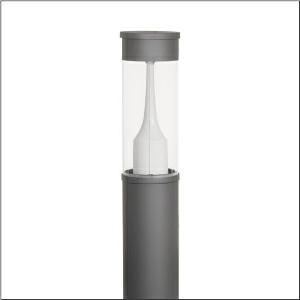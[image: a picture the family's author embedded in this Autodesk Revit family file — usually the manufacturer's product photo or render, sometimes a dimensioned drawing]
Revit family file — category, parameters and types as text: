
# Revit family: city-light_400_iq___st1_2a_5xa5305kf14h_7e7c
name_source: partatom
category: Lighting Fixtures
units: mm (PartAtom-declared; Revit-internal decimal feet)

## family parameters
Cut with Voids When Loaded = No
Host = Face
Light Source = No
Part Type = Normal
Room Calculation Point = No
Round Connector Dimension = Use Diameter
Shared = No

## types (1)
- --- (1 x LED, 1540 lm, 10 W, 4000K)
    Apparent Load = 10 VA
    CIE Flux Codes = 22 61 93 96 100
    Color Rendering = 70
    Color Temperature = 4000K
    Default Elevation = 1800 mm
    Description = City-Light 400 iQ, light pillar, Module 540 iQ-SR, primary light control with 3 zone facetted reflector, of plastic, silver coated, highly specular, structured, primary optical cover: cover, of PMMA, transparent, partly coated, light distribution: ST1.2a, primary light characteristic: asymmetric, LED, High Power LED, rated luminous flux: 1.540lm, luminous efficacy: 154lm/W, light colour: 740, colour temperature: 4000K, control gear: iQ Street-Remote, control: pre-setting: logarithmic dimming characteristic, Street-Remote, Auto-Match, Temp-Guard, Lumen-Switch, Night-Set, Smart-Wire, Light-Fading, Desk-Remote (wireless, voltage-free reading and setting of iQ features in the workshop via application-optimized NFC function/RFID function), optimised constant luminous flux control (CLO 2.0), with terminal, 6-pole, max. 2.5mm², mains connection: 230..240V, AC, 50/60Hz, start of lifetime: 10W, end of service life: 10W, reduction: 5W, luminaire housing, cylindrical, of extruded aluminium section, coated, Siteco® metallic grey (DB 702S), length: 4.694mm, diameter: 200mm, Module 540 iQ-SR, traffic white (RAL 9016), equipment: standard, protection rating (complete): IP65, insulation class (complete): insulation class II (safety insulation), certification: CE, ENEC, VDE, packaging unit: 1 piece

Light Distribution: ST1.2a
    Height = 500 mm
    Lamp = 1 x LED
    Lamp Light Flux = 1540 lm
    Lamp Power = 10 W
    Lamp count = 1
    Length = 200 mm  [stored 0.656168 ft]
    Luminous efficacy = 154 lm/W
    Manufacturer = Siteco
    ModVariant = No
    Model = 5XA5305KF14H
    Mounting Place = Floor
    Mounting Type = Freestanding
    Number of Poles = 1
    OnlyDefault = Yes
    Power Factor = 1
    Product Name = City-Light 400 iQ | ST1.2a
    Product group = light pillar
    ProductGroupID = 1301
    Protection Class = Protection class II
    Protection Degree = IP 65
    RLX_Detail_Level = 1
    RLX_Emergency_Light_Flux = 0 lm
    RLX_Emergency_Type = 0
    RLX_Emergency_Type_DB = No
    RlxData = <blob elided: 87093 chars, md5=843592f7>
    Socket = socket
    Standby Power = 0 W
    System Light Flux = 1540 lm
    System Power = 10 W
    Type Comments = factory setting: luminous flux: 100 % | dim-lin: 254 | 401 mA
    Type Image = l_1006914.jpg
    URL = http://relux.com
    VarID = @adj_160107
    Voltage = 0 V
    Weight = 0.00 kg
    Width = 0 mm  [stored 0 ft]

note: [stored X ft] marks values corroborated as IEEE doubles in the binary element streams (Revit-internal decimal feet)

## geometry (parser evidence)
native form markers: Blend x4, Sweep x11
no freeform markers — native parametric forms only
